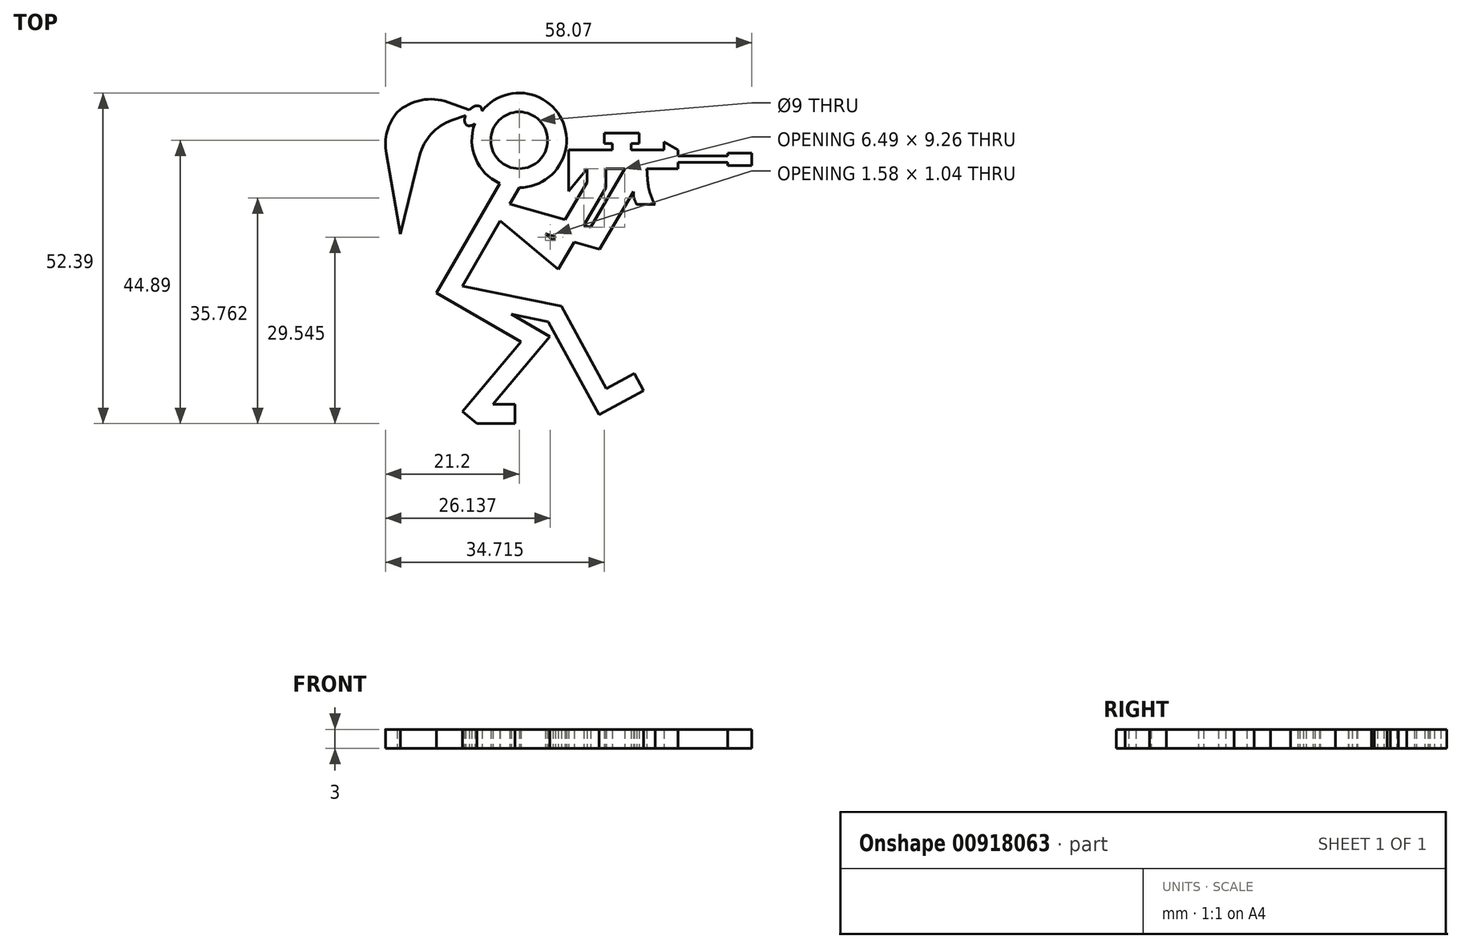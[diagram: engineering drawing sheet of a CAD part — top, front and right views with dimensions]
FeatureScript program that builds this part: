
annotation { "Feature Type Name" : "Feature", "Feature Type Description" : "" }
export const myFeature = defineFeature(function(context is Context, id is Id, definition is map)
    precondition{}
    {
        {
            var Q0;
            Q0=qCreatedBy(makeId("Top.planeOp"),FACE);
            var sketch = newSketch(context, id + "F0", { "sketchPlane" : qUnion([Q0])});
            skCircle(sketch, "E0", {"center": v(0, 0) * mm, "radius": 7.5 * mm});
            skCircle(sketch, "E1.0", {"center": v(0, 0) * mm, "radius": 4.5 * mm});
            skLineSegment(sketch, "E2", {"start": v(0, -7.5) * mm, "end": v(-10.5, -25.7) * mm});
            skLineSegment(sketch, "E3", {"start": v(-10.5, -25.7) * mm, "end": v(-13.1, -24.2) * mm});
            skLineSegment(sketch, "E4", {"start": v(-13.1, -24.2) * mm, "end": v(-3.08, -6.84) * mm});
            skLineSegment(sketch, "E5", {"start": v(0, -7.5) * mm, "end": v(0, -12.14) * mm, "construction": true});
            skLineSegment(sketch, "E6", {"start": v(-10.5, -25.7) * mm, "end": v(0.27, -31.9) * mm});
            skLineSegment(sketch, "E7", {"start": v(0.27, -31.9) * mm, "end": v(-9, -42.96) * mm});
            skLineSegment(sketch, "E8", {"start": v(-9, -42.96) * mm, "end": v(-6.7, -44.89) * mm});
            skLineSegment(sketch, "E9", {"start": v(-6.7, -44.89) * mm, "end": v(4.87, -31.1) * mm});
            skLineSegment(sketch, "E10", {"start": v(4.87, -31.1) * mm, "end": v(-9, -23.1) * mm});
            skLineSegment(sketch, "E11", {"start": v(-10.5, -25.7) * mm, "end": v(4.62, -28.75) * mm});
            skLineSegment(sketch, "E12", {"start": v(4.62, -28.75) * mm, "end": v(12.65, -43.5) * mm});
            skLineSegment(sketch, "E13", {"start": v(12.65, -43.5) * mm, "end": v(15.29, -42.07) * mm});
            skLineSegment(sketch, "E14", {"start": v(15.29, -42.07) * mm, "end": v(6.68, -26.26) * mm});
            skLineSegment(sketch, "E15", {"start": v(6.68, -26.26) * mm, "end": v(-9, -23.1) * mm});
            skLineSegment(sketch, "E16", {"start": v(-1.5, -10.1) * mm, "end": v(5.38, -15.86) * mm});
            skLineSegment(sketch, "E17", {"start": v(5.38, -15.86) * mm, "end": v(10.76, -6.69) * mm});
            skLineSegment(sketch, "E18", {"start": v(10.76, -6.69) * mm, "end": v(10.76, -4.5) * mm});
            skLineSegment(sketch, "E19", {"start": v(10.76, -4.5) * mm, "end": v(13.76, -4.5) * mm});
            skLineSegment(sketch, "E20", {"start": v(13.76, -4.5) * mm, "end": v(13.76, -7.5) * mm});
            skLineSegment(sketch, "E21", {"start": v(13.76, -7.5) * mm, "end": v(6.18, -20.44) * mm});
            skLineSegment(sketch, "E22", {"start": v(6.18, -20.44) * mm, "end": v(-3.02, -12.74) * mm});
            skLineSegment(sketch, "E23", {"start": v(4.15, -14.83) * mm, "end": v(12.74, -17.28) * mm});
            skLineSegment(sketch, "E24", {"start": v(12.74, -17.28) * mm, "end": v(20.24, -4.5) * mm});
            skLineSegment(sketch, "E25", {"start": v(20.24, -4.5) * mm, "end": v(16.76, -4.5) * mm});
            skLineSegment(sketch, "E26", {"start": v(16.76, -4.5) * mm, "end": v(11.33, -13.76) * mm});
            skLineSegment(sketch, "E27", {"start": v(11.33, -13.76) * mm, "end": v(-1.5, -10.1) * mm});
            skLineSegment(sketch, "E28.bottom", {"start": v(8.76, -4.5) * mm, "end": v(25.16, -4.5) * mm});
            skLineSegment(sketch, "E28.top", {"start": v(8.76, -1.5) * mm, "end": v(25.16, -1.5) * mm});
            skLineSegment(sketch, "E28.left", {"start": v(8.76, -4.5) * mm, "end": v(8.76, -1.5) * mm});
            skLineSegment(sketch, "E28.right", {"start": v(25.16, -4.5) * mm, "end": v(25.16, -1.5) * mm});
            skLineSegment(sketch, "E29.bottom", {"start": v(14.76, -1.5) * mm, "end": v(17.76, -1.5) * mm});
            skLineSegment(sketch, "E29.top", {"start": v(14.76, -0.5) * mm, "end": v(17.76, -0.5) * mm});
            skLineSegment(sketch, "E29.left", {"start": v(14.76, -1.5) * mm, "end": v(14.76, -0.5) * mm});
            skLineSegment(sketch, "E29.right", {"start": v(17.76, -1.5) * mm, "end": v(17.76, -0.5) * mm});
            skLineSegment(sketch, "E30", {"start": v(25.16, -1.5) * mm, "end": v(22.94, -0.24) * mm});
            skLineSegment(sketch, "E31", {"start": v(22.94, -0.24) * mm, "end": v(22.94, -1.5) * mm});
            skPoint(sketch, "E32.orphan", {"position": v(8.7, -16.13) * mm});
            skEllipse(sketch, "E33", {"center": v(-7.28, 3.9) * mm, "majorRadius": 1.81 * mm, "minorRadius": 1.08 * mm, "majorAxis": v(0.59, 0.8)});
            skLineSegment(sketch, "E34", {"start": v(-7.9, 4.83) * mm, "end": v(-16.16, 7.8) * mm});
            skLineSegment(sketch, "E35", {"start": v(-16.16, 7.8) * mm, "end": v(-21.8, 1.94) * mm});
            skLineSegment(sketch, "E36", {"start": v(-21.8, 1.94) * mm, "end": v(-18.81, -14.84) * mm});
            skLineSegment(sketch, "E37", {"start": v(-18.81, -14.84) * mm, "end": v(-16.27, -4.46) * mm});
            skLineSegment(sketch, "E38", {"start": v(-16.27, -4.46) * mm, "end": v(-14.73, 1.72) * mm});
            skLineSegment(sketch, "E39", {"start": v(-14.73, 1.72) * mm, "end": v(-8.48, 3.95) * mm});
            skLineSegment(sketch, "E40.bottom", {"start": v(25.16, -2.49) * mm, "end": v(33.07, -2.49) * mm});
            skLineSegment(sketch, "E40.top", {"start": v(25.16, -3.5) * mm, "end": v(33.07, -3.5) * mm});
            skLineSegment(sketch, "E40.left", {"start": v(25.16, -2.49) * mm, "end": v(25.16, -3.5) * mm});
            skLineSegment(sketch, "E40.right", {"start": v(33.07, -2.49) * mm, "end": v(33.07, -3.5) * mm});
            skLineSegment(sketch, "E41.bottom", {"start": v(33.07, -2.02) * mm, "end": v(36.87, -2.02) * mm});
            skLineSegment(sketch, "E41.top", {"start": v(33.07, -4) * mm, "end": v(36.87, -4) * mm});
            skLineSegment(sketch, "E41.left", {"start": v(33.07, -2.02) * mm, "end": v(33.07, -4) * mm});
            skLineSegment(sketch, "E41.right", {"start": v(36.87, -2.02) * mm, "end": v(36.87, -4) * mm});
            skFitSpline(sketch, "E42", {"points": [v(20.24, -4.5) * mm, v(21.52, -10.2) * mm], "startDerivative": vector(0.3, -5.2) * mm, "endDerivative": vector(3.47, -5.85) * mm});
            skFitSpline(sketch, "E43", {"points": [v(18.1, -8.15) * mm, v(18.63, -10.2) * mm], "startDerivative": vector(-0.15, -2.57) * mm, "endDerivative": vector(0.89, -1.95) * mm});
            skLineSegment(sketch, "E44", {"start": v(18.63, -10.2) * mm, "end": v(21.52, -10.2) * mm});
            skLineSegment(sketch, "E45", {"start": v(8.76, -1.5) * mm, "end": v(7.83, -1.5) * mm});
            skLineSegment(sketch, "E46", {"start": v(7.83, -1.5) * mm, "end": v(7.83, -8.06) * mm});
            skLineSegment(sketch, "E47", {"start": v(7.83, -8.06) * mm, "end": v(10.76, -4.5) * mm});
            skLineSegment(sketch, "E48.bottom", {"start": v(13.46, -0.5) * mm, "end": v(19.01, -0.5) * mm});
            skLineSegment(sketch, "E48.top", {"start": v(13.46, 1.13) * mm, "end": v(19.01, 1.13) * mm});
            skLineSegment(sketch, "E48.left", {"start": v(13.46, -0.5) * mm, "end": v(13.46, 1.13) * mm});
            skLineSegment(sketch, "E48.right", {"start": v(19.01, -0.5) * mm, "end": v(19.01, 1.13) * mm});
            skLineSegment(sketch, "E49", {"start": v(-6.7, -44.89) * mm, "end": v(-0.67, -44.89) * mm});
            skLineSegment(sketch, "E50", {"start": v(-0.67, -44.89) * mm, "end": v(-0.67, -41.82) * mm});
            skLineSegment(sketch, "E51", {"start": v(-0.67, -41.82) * mm, "end": v(-4.13, -41.82) * mm});
            skLineSegment(sketch, "E52", {"start": v(15.29, -42.07) * mm, "end": v(19.71, -39.66) * mm});
            skLineSegment(sketch, "E53", {"start": v(19.71, -39.66) * mm, "end": v(18.25, -36.98) * mm});
            skLineSegment(sketch, "E54", {"start": v(18.25, -36.98) * mm, "end": v(13.83, -39.39) * mm});
            skSolve(sketch);
        }
        {
            var Q0;
            {var subQ0=sQuery(id+"F0.wireOp",EDGE,"E17");var subQ5=sQuery(id+"F0.wireOp",EDGE,"E27");var subQ10=sQuery(id+"F0.wireOp",EDGE,"E22");var subQ16=sQuery(id+"F0.wireOp",EDGE,"E12");var subQ17=sQuery(id+"F0.wireOp",EDGE,"E11");var subQ18=sQuery(id+"F0.wireOp",EDGE,"E10");var subQ19=makeQuery(id+"F0.imprint","INTERSECT",VERTEX,{"derivedFrom":[subQ18,subQ17]});var subQ23=makeQuery(id+"F0.imprint","IMPRINT",EDGE,{"disambiguationData":[TD([[subQ19,-1.0]])],"derivedFrom":subQ18});var subQ27=sQuery(id+"F0.wireOp",EDGE,"E52");var subQ29=sQuery(id+"F0.wireOp",EDGE,"E30");var subQ36=makeQuery(id+"F0.imprint","INTERSECT",VERTEX,{"derivedFrom":[subQ0,subQ5]});var subQ37=makeQuery(id+"F0.imprint","IMPRINT",EDGE,{"disambiguationData":[TD([[subQ36,1.0]])],"derivedFrom":subQ0});var subQ46=sQuery(id+"F0.wireOp",EDGE,"E6");var subQ47=sQuery(id+"F0.wireOp",EDGE,"E49");var subQ49=sQuery(id+"F0.wireOp",EDGE,"E3");var subQ52=sQuery(id+"F0.wireOp",EDGE,"E0");var subQ54=sQuery(id+"F0.wireOp",EDGE,"E33");var subQ59=makeQuery(id+"F0.imprint","INTERSECT",VERTEX,{"disambiguationData":[OD(0.0)],"derivedFrom":[subQ52,subQ54]});var subQ66=sQuery(id+"F0.wireOp",EDGE,"E29.top");var subQ67=makeQuery(id+"F0.imprint","IMPRINT",EDGE,{"derivedFrom":subQ66});var subQ69=sQuery(id+"F0.wireOp",EDGE,"E28.left");var subQ70=makeQuery(id+"F0.imprint","IMPRINT",EDGE,{"derivedFrom":subQ69});var subQ73=sQuery(id+"F0.wireOp",EDGE,"E19");var subQ74=sQuery(id+"F0.wireOp",EDGE,"E18");var subQ76=sQuery(id+"F0.wireOp",EDGE,"E42");var subQ77=sQuery(id+"F0.wireOp",EDGE,"E25");var subQ85=makeQuery(id+"F0.imprint","IMPRINT",EDGE,{"derivedFrom":subQ77});var subQ86=makeQuery(id+"F0.imprint","IMPRINT",EDGE,{"disambiguationData":[TD([[subQ59,1.0]])],"derivedFrom":subQ52});var subQ88=makeQuery(id+"F0.imprint","IMPRINT",EDGE,{"derivedFrom":subQ73});var subQ93=sQuery(id+"F0.wireOp",EDGE,"E40.bottom");var subQ96=sQuery(id+"F0.wireOp",EDGE,"E34");var subQ101=sQuery(id+"F0.wireOp",EDGE,"E40.right");var subQ102=makeQuery(id+"F0.imprint","IMPRINT",EDGE,{"derivedFrom":subQ101});Q0=qUnion([makeQuery(id+"F0.imprint","IMPRINT",FACE,{"disambiguationData":[TD([[subQ67,1.0]])]}),makeQuery(id+"F0.imprint","IMPRINT",FACE,{"disambiguationData":[TD([[makeQuery(id+"F0.imprint","IMPRINT",EDGE,{"derivedFrom":subQ74}),-1.0]])]}),makeQuery(id+"F0.imprint","IMPRINT",FACE,{"disambiguationData":[TD([[makeQuery(id+"F0.imprint","IMPRINT",EDGE,{"derivedFrom":subQ96}),1.0]])]}),makeQuery(id+"F0.imprint","IMPRINT",FACE,{"disambiguationData":[TD([[makeQuery(id+"F0.imprint","IMPRINT",EDGE,{"derivedFrom":subQ47}),1.0]])]}),makeQuery(id+"F0.imprint","IMPRINT",FACE,{"disambiguationData":[TD([[subQ37,1.0]])]}),makeQuery(id+"F0.imprint","IMPRINT",FACE,{"disambiguationData":[TD([[subQ102,1.0]])]}),makeQuery(id+"F0.imprint","IMPRINT",FACE,{"disambiguationData":[TD([[makeQuery(id+"F0.imprint","IMPRINT",EDGE,{"derivedFrom":subQ27}),1.0]])]}),makeQuery(id+"F0.imprint","IMPRINT",FACE,{"disambiguationData":[TD([[makeQuery(id+"F0.imprint","IMPRINT",EDGE,{"derivedFrom":subQ93}),-1.0]])]}),makeQuery(id+"F0.imprint","IMPRINT",FACE,{"disambiguationData":[TD([[subQ23,1.0]])]}),makeQuery(id+"F0.imprint","IMPRINT",FACE,{"disambiguationData":[TD([[subQ86,-1.0]])]}),makeQuery(id+"F0.imprint","IMPRINT",FACE,{"disambiguationData":[TD([[subQ88,1.0]])]}),makeQuery(id+"F0.imprint","IMPRINT",FACE,{"disambiguationData":[TD([[makeQuery(id+"F0.imprint","IMPRINT",EDGE,{"derivedFrom":subQ76}),-1.0]])]}),makeQuery(id+"F0.imprint","IMPRINT",FACE,{"disambiguationData":[TD([[makeQuery(id+"F0.imprint","IMPRINT",EDGE,{"derivedFrom":subQ49}),-1.0]])]}),makeQuery(id+"F0.imprint","IMPRINT",FACE,{"disambiguationData":[TD([[subQ86,1.0]])]}),makeQuery(id+"F0.imprint","IMPRINT",FACE,{"disambiguationData":[TD([[subQ85,1.0]])]}),makeQuery(id+"F0.imprint","IMPRINT",FACE,{"disambiguationData":[TD([[subQ70,1.0]])]}),makeQuery(id+"F0.imprint","IMPRINT",FACE,{"disambiguationData":[TD([[subQ67,-1.0]])]}),makeQuery(id+"F0.imprint","IMPRINT",FACE,{"disambiguationData":[TD([[makeQuery(id+"F0.imprint","IMPRINT",EDGE,{"derivedFrom":sQuery(id+"F0.wireOp",EDGE,"E1.0")}),-1.0]])]}),makeQuery(id+"F0.imprint","IMPRINT",FACE,{"disambiguationData":[TD([[makeQuery(id+"F0.imprint","IMPRINT",EDGE,{"derivedFrom":subQ46}),1.0]])]}),makeQuery(id+"F0.imprint","IMPRINT",FACE,{"disambiguationData":[TD([[subQ37,-1.0]])]}),makeQuery(id+"F0.imprint","IMPRINT",FACE,{"disambiguationData":[TD([[makeQuery(id+"F0.imprint","IMPRINT",EDGE,{"derivedFrom":subQ29}),1.0]])]}),makeQuery(id+"F0.imprint","IMPRINT",FACE,{"disambiguationData":[TD([[makeQuery(id+"F0.imprint","IMPRINT",EDGE,{"derivedFrom":subQ16}),1.0]])]}),makeQuery(id+"F0.imprint","IMPRINT",FACE,{"disambiguationData":[TD([[makeQuery(id+"F0.imprint","IMPRINT",EDGE,{"derivedFrom":subQ10}),-1.0]])]})]);}
            extrude(context, id + "F1", {"entities" : qUnion([Q0]), "depth" : 3 * mm, "offsetDistance" : 25 * mm});
        }
        {
            var Q0;
            Q0=makeQuery(id+"F1.opExtrude","SWEPT_EDGE",EDGE,{"disambiguationData":[OSD([sQuery(id+"F0.wireOp",EDGE,"E34"),sQuery(id+"F0.wireOp",EDGE,"E35")])]});
            var Q1;
            Q1=makeQuery(id+"F1.opExtrude","SWEPT_EDGE",EDGE,{"disambiguationData":[OSD([sQuery(id+"F0.wireOp",EDGE,"E35"),sQuery(id+"F0.wireOp",EDGE,"E36")])]});
            var Q2;
            Q2=makeQuery(id+"F1.opExtrude","SWEPT_EDGE",EDGE,{"disambiguationData":[OSD([sQuery(id+"F0.wireOp",EDGE,"E38"),sQuery(id+"F0.wireOp",EDGE,"E39")])]});
            fillet(context, id + "F2", {"entities" : qUnion([Q0, Q1, Q2]), "radius" : 8 * mm, "tangentPropagation" : true, "allowEdgeOverflow" : false});
        }
    });
